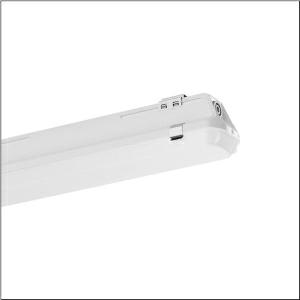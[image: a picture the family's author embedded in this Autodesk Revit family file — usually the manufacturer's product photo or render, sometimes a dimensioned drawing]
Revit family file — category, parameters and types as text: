
# Revit family: monsun_r__21_51fb107p420b_fb8a
name_source: partatom
category: Lighting Fixtures
units: mm (PartAtom-declared; Revit-internal decimal feet)

## family parameters
Cut with Voids When Loaded = No
Host = Face
Light Source = No
Part Type = Normal
Room Calculation Point = No
Round Connector Dimension = Use Diameter
Shared = No

## types (1)
- Monsun® 21 (1 x LED, 2580 lm, 17.5 W, 4000K)
    Apparent Load = 18 VA
    CIE Flux Codes = 47 77 93 94 100
    Color Rendering = 80
    Color Temperature = 4000K
    Default Elevation = 1800 mm
    Description = Monsun® 21, damp-proof luminaire, chain hanger, primary optical cover: enclosure, of PMMA, light emission: direct distribution, primary light characteristic: symmetric, installation type: suspended mounting, surface-mounted, horizontal mounting, vertical mounting, LED, rated luminous flux: 2.580lm, luminous efficacy: 147lm/W, light colour: 840, colour temperature: 4000K, control gear: ECG, with terminal, 3-pole, max. 2.5mm², mains connection: 220..240V, AC, 50/60Hz, rated input power: 18W, housing, of glass-fibre reinforced polyester, uncoated, bright grey, incl. chain hanger, length: 1.590mm, width: 90mm, height: 88mm, clip for enclosure, of stainless steel (V2A), ceiling mounting element, of stainless steel (V2A), chain hanger, of stainless steel (V2A), protection rating (complete): IP66, insulation class (complete): insulation class I (protective earthing), certification: CE, ENEC, VDE, UKCA, protection symbol: D, impact resistance: IK04, permissible operating ambient temperature: -25..+35°C, standard: EN 50419, EN 60598-2-1, corresponds to IFS (International Featured Standards) requirements for safety and quality in the food industry, for indoor or canopied outdoor use, no direct snow, no direct sun, no direct rain, contact your sales advisor before using the luminaires in applications with unclear chemical exposure, large temperature fluctuations or condensation-forming humidity, LABS conformity tested according to VDMA 24364:2018-05, packaging unit: 1 piece
    Height = 89 mm
    Lamp = 1 x LED
    Lamp Light Flux = 2580 lm
    Lamp Power = 17.5 W
    Lamp count = 1
    Length = 1590 mm
    Luminous efficacy = 147 lm/W
    Manufacturer = Siteco
    ModVariant = No
    Model = 51FB107P420B
    Mounting Place = Ceiling
    Mounting Type = Surface mounted
    Number of Poles = 1
    OnlyDefault = Yes
    Power Factor = 1
    Product Name = Monsun® 21
    Product group = damp-proof luminaire
    ProductGroupID = 300
    Protection Class = Protection class I
    Protection Degree = IP 66
    RLX_Detail_Level = 1
    RLX_Emergency_Light_Flux = 0 lm
    RLX_Emergency_Type = 0
    RLX_Emergency_Type_DB = No
    RlxData = <blob elided: 88481 chars, md5=889743f1>
    Socket = socket
    Standby Power = 0 W
    System Light Flux = 2580 lm
    System Power = 18 W
    Type Comments = Product without accessories
    Type Image = l_1319656.jpg
    URL = http://relux.com
    VarID = ---
    Voltage = 0 V
    Weight = 0.00 kg
    Width = 90 mm

## geometry (parser evidence)
native form markers: Blend x4, Sweep x13
no freeform markers — native parametric forms only
